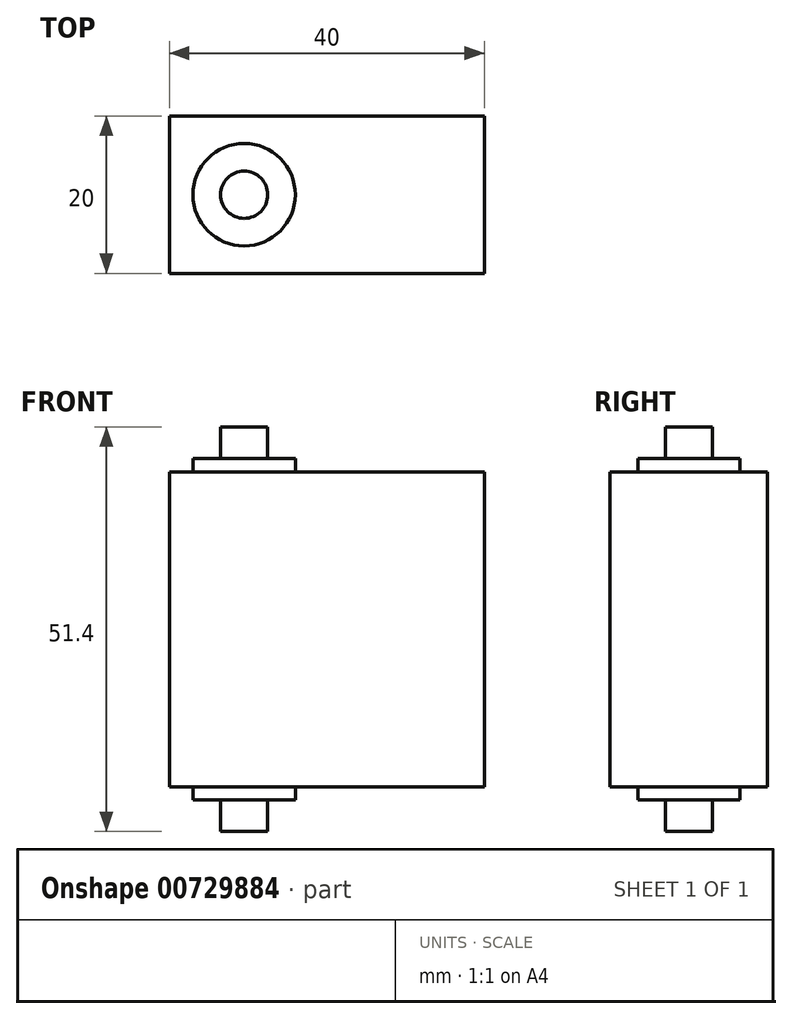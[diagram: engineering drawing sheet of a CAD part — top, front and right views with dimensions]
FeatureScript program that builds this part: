
annotation { "Feature Type Name" : "Feature", "Feature Type Description" : "" }
export const myFeature = defineFeature(function(context is Context, id is Id, definition is map)
    precondition{}
    {
        {
            var Q0;
            Q0=qCreatedBy(makeId("Top.planeOp"),FACE);
            var sketch = newSketch(context, id + "F0", { "sketchPlane" : qUnion([Q0])});
            skLineSegment(sketch, "E0.bottom", {"start": v(0, 0) * mm, "end": v(40, 0) * mm});
            skLineSegment(sketch, "E0.top", {"start": v(0, 20) * mm, "end": v(40, 20) * mm});
            skLineSegment(sketch, "E0.left", {"start": v(0, 0) * mm, "end": v(0, 20) * mm});
            skLineSegment(sketch, "E0.right", {"start": v(40, 0) * mm, "end": v(40, 20) * mm});
            skSolve(sketch);
        }
        {
            var Q0;
            Q0=makeQuery(id+"F0.imprint","IMPRINT",FACE,{"disambiguationData":[TD([[makeQuery(id+"F0.imprint","IMPRINT",EDGE,{"derivedFrom":sQuery(id+"F0.wireOp",EDGE,"E0.bottom")}),1.0]])]});
            extrude(context, id + "F1", {"entities" : qUnion([Q0]), "depth" : 40 * mm, "offsetDistance" : 25 * mm});
        }
        {
            var Q0;
            Q0=makeQuery(id+"F1.opExtrude","CAP_FACE",FACE,{"disambiguationData":[OSD([sQuery(id+"F0.wireOp",EDGE,"E0.bottom"),sQuery(id+"F0.wireOp",EDGE,"E0.top"),sQuery(id+"F0.wireOp",EDGE,"E0.left"),sQuery(id+"F0.wireOp",EDGE,"E0.right")])],"isStart":false});
            var sketch = newSketch(context, id + "F2", { "sketchPlane" : qUnion([Q0])});
            skLineSegment(sketch, "E1", {"start": v(9.5, 20) * mm, "end": v(9.5, 0) * mm, "construction": true});
            skCircle(sketch, "E2", {"center": v(9.5, 10) * mm, "radius": 6.5 * mm});
            skSolve(sketch);
        }
        {
            var Q0;
            Q0=makeQuery(id+"F2.imprint","IMPRINT",FACE,{"disambiguationData":[TD([[makeQuery(id+"F2.imprint","IMPRINT",EDGE,{"derivedFrom":sQuery(id+"F2.wireOp",EDGE,"E2")}),1.0]])]});
            extrude(context, id + "F3", {"entities" : qUnion([Q0]), "operationType" : NewBodyOperationType.ADD, "depth" : 1.7 * mm, "offsetDistance" : 25 * mm});
        }
        {
            var Q0;
            Q0=makeQuery(id+"F3.opExtrude","CAP_FACE",FACE,{"disambiguationData":[OSD([sQuery(id+"F2.wireOp",EDGE,"E2")])],"isStart":false});
            var sketch = newSketch(context, id + "F4", { "sketchPlane" : qUnion([Q0])});
            skCircle(sketch, "E3", {"center": v(9.5, 10) * mm, "radius": 3 * mm});
            skSolve(sketch);
        }
        {
            var Q0;
            Q0=makeQuery(id+"F4.imprint","IMPRINT",FACE,{"disambiguationData":[TD([[makeQuery(id+"F4.imprint","IMPRINT",EDGE,{"derivedFrom":sQuery(id+"F4.wireOp",EDGE,"E3")}),1.0]])]});
            extrude(context, id + "F5", {"entities" : qUnion([Q0]), "operationType" : NewBodyOperationType.ADD, "depth" : 4 * mm, "offsetDistance" : 25 * mm});
        }
        {
            var Q0;
            Q0=makeQuery(id+"F1.opExtrude","CAP_FACE",FACE,{"disambiguationData":[OSD([sQuery(id+"F0.wireOp",EDGE,"E0.bottom"),sQuery(id+"F0.wireOp",EDGE,"E0.top"),sQuery(id+"F0.wireOp",EDGE,"E0.left"),sQuery(id+"F0.wireOp",EDGE,"E0.right")])],"isStart":true});
            var sketch = newSketch(context, id + "F6", { "sketchPlane" : qUnion([Q0])});
            skLineSegment(sketch, "E4", {"start": v(9.5, 0) * mm, "end": v(9.5, -20) * mm, "construction": true});
            skCircle(sketch, "E5", {"center": v(9.5, -10) * mm, "radius": 6.5 * mm});
            skSolve(sketch);
        }
        {
            var Q0;
            Q0=makeQuery(id+"F6.imprint","IMPRINT",FACE,{"disambiguationData":[TD([[makeQuery(id+"F6.imprint","IMPRINT",EDGE,{"derivedFrom":sQuery(id+"F6.wireOp",EDGE,"E5")}),1.0]])]});
            extrude(context, id + "F7", {"entities" : qUnion([Q0]), "operationType" : NewBodyOperationType.ADD, "depth" : 1.7 * mm, "offsetDistance" : 25 * mm});
        }
        {
            var Q0;
            Q0=makeQuery(id+"F7.opExtrude","CAP_FACE",FACE,{"disambiguationData":[OSD([sQuery(id+"F6.wireOp",EDGE,"E5")])],"isStart":false});
            var sketch = newSketch(context, id + "F8", { "sketchPlane" : qUnion([Q0])});
            skCircle(sketch, "E6", {"center": v(9.5, -10) * mm, "radius": 3 * mm});
            skSolve(sketch);
        }
        {
            var Q0;
            Q0=makeQuery(id+"F8.imprint","IMPRINT",FACE,{"disambiguationData":[TD([[makeQuery(id+"F8.imprint","IMPRINT",EDGE,{"derivedFrom":sQuery(id+"F8.wireOp",EDGE,"E6")}),1.0]])]});
            extrude(context, id + "F9", {"entities" : qUnion([Q0]), "operationType" : NewBodyOperationType.ADD, "depth" : 4 * mm, "offsetDistance" : 25 * mm});
        }
    });
